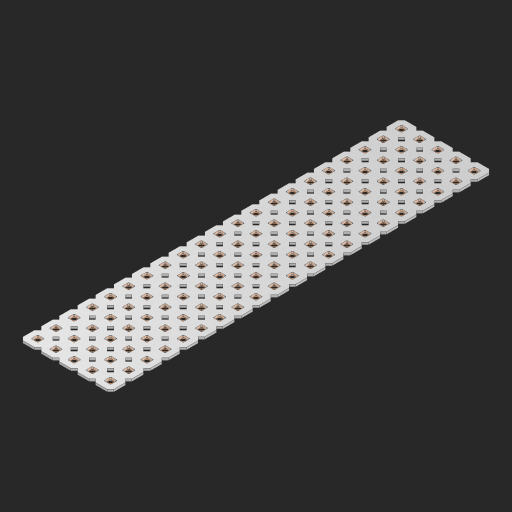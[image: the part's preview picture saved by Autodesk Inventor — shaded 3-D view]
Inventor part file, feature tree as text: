
AUTODESK INVENTOR PART (.ipt)
format: ipt  version: 2023 (Build 270158000, 158)  size: 1,501,184 bytes
history: native  units: in
note: dims shown in document units (in); Inventor stores cm internally (conversion verified against a paired STEP export)
features: other x106, extrude x104, sketch x2, pattern_linear x1
ambient origin geometry x8: Origin, YZ Plane, XZ Plane, XY Plane, X Axis, Y Axis, Z Axis, Center Point
bodies: Solid1 (feature_tree), Body (feature_tree)
feature tree (213):
  pattern_linear  "Rectangular Pattern1"  Spacing1=0.09in  [1 undecoded]
  sketch  "Sketch1"  dims[d1=0.5in]
  sketch  "Sketch2"  dims[d2=0.182in d3=0.09in d4=0.09in d5=0.09in d6=0.09in d7=0.09in d8=0.09in d9=0.09in d10=0.09in d11=0.02in d13=0.0in d14=0.172in d15=0.0625in d16=0.0in d19=0.5in d22=0.5in]
  other  "Srf1"
  other  "Srf126"
  other  "Srf127"
  other  "Srf128"
  other  "Srf129"
  other  "Srf130"
  other  "Srf131"
  other  "Srf250"
  other  "Srf251"
  other  "Srf252"
  other  "Srf253"
  other  "Srf254"
  other  "Srf255"
  other  "Srf256"
  other  "Srf257"
  other  "Srf258"
  other  "Srf259"
  other  "Srf260"
  other  "Srf261"
  other  "Srf262"
  other  "Srf263"
  other  "Srf268"
  other  "Srf269"
  other  "Srf270"
  other  "Srf271"
  other  "Srf272"
  other  "Srf273"
  other  "Srf274"
  other  "Srf275"
  other  "Srf276"
  other  "Srf277"
  other  "Srf278"
  other  "Srf279"
  other  "Srf280"
  other  "Srf281"
  other  "Srf282"
  other  "Srf283"
  other  "Srf284"
  other  "Srf285"
  other  "Srf286"
  other  "Srf287"
  other  "Srf288"
  other  "Srf293"
  other  "Srf294"
  other  "Srf295"
  other  "Srf296"
  other  "Srf297"
  other  "Srf298"
  other  "Srf299"
  other  "Srf300"
  other  "Srf301"
  other  "Srf302"
  other  "Srf303"
  other  "Srf304"
  other  "Srf305"
  other  "Srf306"
  other  "Srf307"
  other  "Srf308"
  other  "Srf309"
  other  "Srf310"
  other  "Srf311"
  other  "Srf312"
  other  "Srf313"
  other  "Srf318"
  other  "Srf319"
  other  "Srf320"
  other  "Srf321"
  other  "Srf322"
  other  "Srf323"
  other  "Srf324"
  other  "Srf325"
  other  "Srf326"
  other  "Srf327"
  other  "Srf328"
  other  "Srf329"
  other  "Srf330"
  other  "Srf331"
  other  "Srf332"
  other  "Srf333"
  other  "Srf334"
  other  "Srf335"
  other  "Srf336"
  other  "Srf337"
  other  "Srf338"
  other  "Srf343"
  other  "Srf344"
  other  "Srf345"
  other  "Srf346"
  other  "Srf347"
  other  "Srf348"
  other  "Srf349"
  other  "Srf350"
  other  "Srf351"
  other  "Srf352"
  other  "Srf353"
  other  "Srf354"
  other  "Srf355"
  other  "Srf356"
  other  "Srf357"
  other  "Srf358"
  other  "Srf359"
  other  "Srf360"
  other  "Srf361"
  other  "Srf362"
  other  "Srf363"
  other  "Circle"
  extrude  "ExtrusionSrf126"  Depth=0.09in
  extrude  "ExtrusionSrf127"  Depth=0.09in
  extrude  "ExtrusionSrf128"  Depth=0.09in
  extrude  "ExtrusionSrf129"  Depth=0.09in
  extrude  "ExtrusionSrf130"  Depth=0.09in
  extrude  "ExtrusionSrf131"  Depth=0.09in
  extrude  "ExtrusionSrf250"  Depth=0.09in
  extrude  "ExtrusionSrf251"  Depth=0.02in
  extrude  "ExtrusionSrf252"  TaperAngle=0.0deg  [1 undecoded]
  extrude  "ExtrusionSrf253"  Depth=0.5in
  extrude  "ExtrusionSrf254"  Depth=0.0625in TaperAngle=0.0deg
  extrude  "ExtrusionSrf255"  Depth=0.5in
  extrude  "ExtrusionSrf256"  Depth=0.5in
  extrude  "ExtrusionSrf257"  [1 undecoded]
  extrude  "ExtrusionSrf258"  [1 undecoded]
  extrude  "ExtrusionSrf259"  [1 undecoded]
  extrude  "ExtrusionSrf260"  [1 undecoded]
  extrude  "ExtrusionSrf261"  [1 undecoded]
  extrude  "ExtrusionSrf262"  [1 undecoded]
  extrude  "ExtrusionSrf263"  [1 undecoded]
  extrude  "ExtrusionSrf268"  [1 undecoded]
  extrude  "ExtrusionSrf269"  [1 undecoded]
  extrude  "ExtrusionSrf270"  [1 undecoded]
  extrude  "ExtrusionSrf271"  [1 undecoded]
  extrude  "ExtrusionSrf272"  [1 undecoded]
  extrude  "ExtrusionSrf273"  [1 undecoded]
  extrude  "ExtrusionSrf274"  [1 undecoded]
  extrude  "ExtrusionSrf275"  [1 undecoded]
  extrude  "ExtrusionSrf276"  [1 undecoded]
  extrude  "ExtrusionSrf277"  [1 undecoded]
  extrude  "ExtrusionSrf278"  [1 undecoded]
  extrude  "ExtrusionSrf279"  [1 undecoded]
  extrude  "ExtrusionSrf280"  [1 undecoded]
  extrude  "ExtrusionSrf281"  [1 undecoded]
  extrude  "ExtrusionSrf282"  [1 undecoded]
  extrude  "ExtrusionSrf283"  [1 undecoded]
  extrude  "ExtrusionSrf284"  [1 undecoded]
  extrude  "ExtrusionSrf285"  [1 undecoded]
  extrude  "ExtrusionSrf286"  [1 undecoded]
  extrude  "ExtrusionSrf287"  [1 undecoded]
  extrude  "ExtrusionSrf288"  [1 undecoded]
  extrude  "ExtrusionSrf293"  [1 undecoded]
  extrude  "ExtrusionSrf294"  [1 undecoded]
  extrude  "ExtrusionSrf295"  [1 undecoded]
  extrude  "ExtrusionSrf296"  [1 undecoded]
  extrude  "ExtrusionSrf297"  [1 undecoded]
  extrude  "ExtrusionSrf298"  [1 undecoded]
  extrude  "ExtrusionSrf299"  [1 undecoded]
  extrude  "ExtrusionSrf300"  [1 undecoded]
  extrude  "ExtrusionSrf301"  [1 undecoded]
  extrude  "ExtrusionSrf302"  [1 undecoded]
  extrude  "ExtrusionSrf303"  [1 undecoded]
  extrude  "ExtrusionSrf304"  [1 undecoded]
  extrude  "ExtrusionSrf305"  [1 undecoded]
  extrude  "ExtrusionSrf306"  [1 undecoded]
  extrude  "ExtrusionSrf307"  [1 undecoded]
  extrude  "ExtrusionSrf308"  [1 undecoded]
  extrude  "ExtrusionSrf309"  [1 undecoded]
  extrude  "ExtrusionSrf310"  [1 undecoded]
  extrude  "ExtrusionSrf311"  [1 undecoded]
  extrude  "ExtrusionSrf312"  [1 undecoded]
  extrude  "ExtrusionSrf313"  [1 undecoded]
  extrude  "ExtrusionSrf318"  [1 undecoded]
  extrude  "ExtrusionSrf319"  [1 undecoded]
  extrude  "ExtrusionSrf320"  [1 undecoded]
  extrude  "ExtrusionSrf321"  [1 undecoded]
  extrude  "ExtrusionSrf322"  [1 undecoded]
  extrude  "ExtrusionSrf323"  [1 undecoded]
  extrude  "ExtrusionSrf324"  [1 undecoded]
  extrude  "ExtrusionSrf325"  [1 undecoded]
  extrude  "ExtrusionSrf326"  [1 undecoded]
  extrude  "ExtrusionSrf327"  [1 undecoded]
  extrude  "ExtrusionSrf328"  [1 undecoded]
  extrude  "ExtrusionSrf329"  [1 undecoded]
  extrude  "ExtrusionSrf330"  [1 undecoded]
  extrude  "ExtrusionSrf331"  [1 undecoded]
  extrude  "ExtrusionSrf332"  [1 undecoded]
  extrude  "ExtrusionSrf333"  [1 undecoded]
  extrude  "ExtrusionSrf334"  [1 undecoded]
  extrude  "ExtrusionSrf335"  [1 undecoded]
  extrude  "ExtrusionSrf336"  [1 undecoded]
  extrude  "ExtrusionSrf337"  [1 undecoded]
  extrude  "ExtrusionSrf338"  [1 undecoded]
  extrude  "ExtrusionSrf343"  [1 undecoded]
  extrude  "ExtrusionSrf344"  [1 undecoded]
  extrude  "ExtrusionSrf345"  [1 undecoded]
  extrude  "ExtrusionSrf346"  [1 undecoded]
  extrude  "ExtrusionSrf347"  [1 undecoded]
  extrude  "ExtrusionSrf348"  [1 undecoded]
  extrude  "ExtrusionSrf349"  [1 undecoded]
  extrude  "ExtrusionSrf350"  [1 undecoded]
  extrude  "ExtrusionSrf351"  [1 undecoded]
  extrude  "ExtrusionSrf352"  [1 undecoded]
  extrude  "ExtrusionSrf353"  [1 undecoded]
  extrude  "ExtrusionSrf354"  [1 undecoded]
  extrude  "ExtrusionSrf355"  [1 undecoded]
  extrude  "ExtrusionSrf356"  [1 undecoded]
  extrude  "ExtrusionSrf357"  [1 undecoded]
  extrude  "ExtrusionSrf358"  [1 undecoded]
  extrude  "ExtrusionSrf359"  [1 undecoded]
  extrude  "ExtrusionSrf360"  [1 undecoded]
  extrude  "ExtrusionSrf361"  [1 undecoded]
  extrude  "ExtrusionSrf362"  [1 undecoded]
  extrude  "ExtrusionSrf363"  [1 undecoded]
note: 93 required parameter values undecoded (feature->parameter linkage not recoverable at this tier; creation-order binding heuristic only, values carry confidence <= 0.55)
